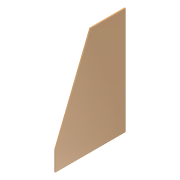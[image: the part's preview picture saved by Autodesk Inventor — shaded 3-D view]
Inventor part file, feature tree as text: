
AUTODESK INVENTOR PART (.ipt)
format: ipt  version: 2014 (Build 180170000, 170)  size: 72,704 bytes
history: native  units: mm
features: extrude x1, sketch x1
ambient origin geometry x8: Origin, YZ Plane, XZ Plane, XY Plane, X Axis, Y Axis, Z Axis, Center Point
bodies: Solid1 (feature_tree)
feature tree (2):
  extrude  "Extrusion1"  Depth=275.0mm
  sketch  "Sketch1"  dims[d0=180.0mm d1=275.0mm d2=90.0mm d3=50.0mm d4=3.0mm d5=0.0mm]
